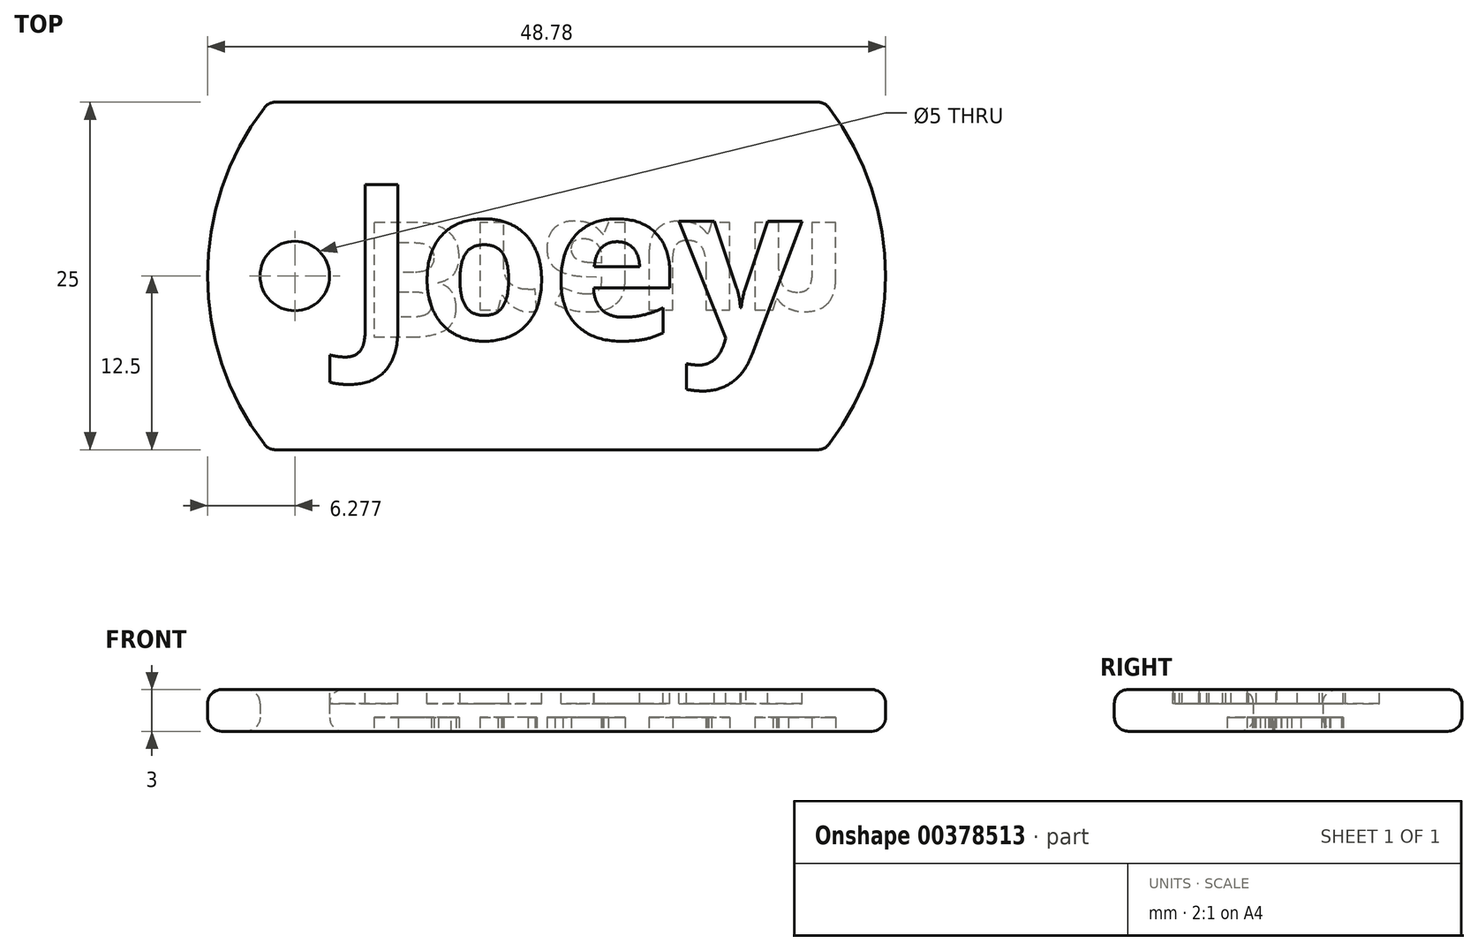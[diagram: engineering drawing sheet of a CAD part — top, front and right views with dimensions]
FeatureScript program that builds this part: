
annotation { "Feature Type Name" : "Feature", "Feature Type Description" : "" }
export const myFeature = defineFeature(function(context is Context, id is Id, definition is map)
    precondition{}
    {
        {
            var Q0;
            Q0=qCreatedBy(makeId("Top.planeOp"),FACE);
            var sketch = newSketch(context, id + "F0", { "sketchPlane" : qUnion([Q0])});
            skLineSegment(sketch, "E0.bottom", {"start": v(-20, 12.5) * mm, "end": v(20, 12.5) * mm});
            skLineSegment(sketch, "E0.top", {"start": v(-20, -12.5) * mm, "end": v(20, -12.5) * mm});
            skArc(sketch, "E1", {"start": v(-20, 12.5) * mm, "mid": v(-24.39, 0) * mm, "end": v(-20, -12.5) * mm});
            skArc(sketch, "E2", {"start": v(20, -12.5) * mm, "mid": v(24.39, 0) * mm, "end": v(20, 12.5) * mm});
            skCircle(sketch, "E3", {"center": v(-18.11, 0) * mm, "radius": 2.5 * mm});
            skSolve(sketch);
        }
        {
            var Q0;
            Q0=makeQuery(id+"F0.imprint","IMPRINT",FACE,{"disambiguationData":[TD([[makeQuery(id+"F0.imprint","IMPRINT",EDGE,{"derivedFrom":sQuery(id+"F0.wireOp",EDGE,"E0.bottom")}),-1.0]])]});
            extrude(context, id + "F1", {"entities" : qUnion([Q0]), "depth" : 3 * mm});
        }
        {
            var Q0;
            Q0=makeQuery(id+"F1.opExtrude","CAP_FACE",FACE,{"disambiguationData":[OSD([sQuery(id+"F0.wireOp",EDGE,"E0.bottom"),sQuery(id+"F0.wireOp",EDGE,"E0.top"),sQuery(id+"F0.wireOp",EDGE,"E1"),sQuery(id+"F0.wireOp",EDGE,"E2"),sQuery(id+"F0.wireOp",EDGE,"E3")])],"isStart":false});
            var sketch = newSketch(context, id + "F2", { "sketchPlane" : qUnion([Q0])});
            skText(sketch, "E4", { "text": "Joey\n", "fontName": "OpenSans-Bold.ttf"});
            const initialGuessF2  = {"E4": [-0.01445, -0.00454, 1, 0, 0.0112]};
            skSetInitialGuess(sketch, initialGuessF2);
            skSolve(sketch);
        }
        {
            var Q0;
            Q0=qSketchRegion(id+"F2",true);
            extrude(context, id + "F3", {"entities" : qUnion([Q0]), "operationType" : NewBodyOperationType.REMOVE, "oppositeDirection" : true, "depth" : 1 * mm});
        }
        {
            var Q0;
            Q0=makeQuery(id+"F1.opExtrude","CAP_FACE",FACE,{"disambiguationData":[OSD([sQuery(id+"F0.wireOp",EDGE,"E0.bottom"),sQuery(id+"F0.wireOp",EDGE,"E0.top"),sQuery(id+"F0.wireOp",EDGE,"E1"),sQuery(id+"F0.wireOp",EDGE,"E2"),sQuery(id+"F0.wireOp",EDGE,"E3")])],"isStart":true});
            var sketch = newSketch(context, id + "F4", { "sketchPlane" : qUnion([Q0])});
            skText(sketch, "E5", { "text": "Braun", "fontName": "OpenSans-Bold.ttf"});
            const initialGuessF4  = {"E5": [-0.01344, -0.00384, 1, 0, 0.0083]};
            skSetInitialGuess(sketch, initialGuessF4);
            skSolve(sketch);
        }
        {
            var Q0;
            Q0=qSketchRegion(id+"F4",true);
            extrude(context, id + "F5", {"entities" : qUnion([Q0]), "operationType" : NewBodyOperationType.REMOVE, "oppositeDirection" : true, "depth" : 1 * mm});
        }
        {
            var Q0;
            Q0=makeQuery(id+"F1.opExtrude","SWEPT_FACE",FACE,{"disambiguationData":[OSD([sQuery(id+"F0.wireOp",EDGE,"E2")])]});
            var Q1;
            Q1=makeQuery(id+"F1.opExtrude","SWEPT_FACE",FACE,{"disambiguationData":[OSD([sQuery(id+"F0.wireOp",EDGE,"E0.top")])]});
            var Q2;
            Q2=makeQuery(id+"F1.opExtrude","SWEPT_FACE",FACE,{"disambiguationData":[OSD([sQuery(id+"F0.wireOp",EDGE,"E3")])]});
            var Q3;
            Q3=makeQuery(id+"F1.opExtrude","SWEPT_FACE",FACE,{"disambiguationData":[OSD([sQuery(id+"F0.wireOp",EDGE,"E1")])]});
            var Q4;
            Q4=makeQuery(id+"F1.opExtrude","SWEPT_FACE",FACE,{"disambiguationData":[OSD([sQuery(id+"F0.wireOp",EDGE,"E0.bottom")])]});
            fillet(context, id + "F6", {"entities" : qUnion([Q0, Q1, Q2, Q3, Q4]), "radius" : 1 * mm, "tangentPropagation" : true, "allowEdgeOverflow" : false});
        }
    });
